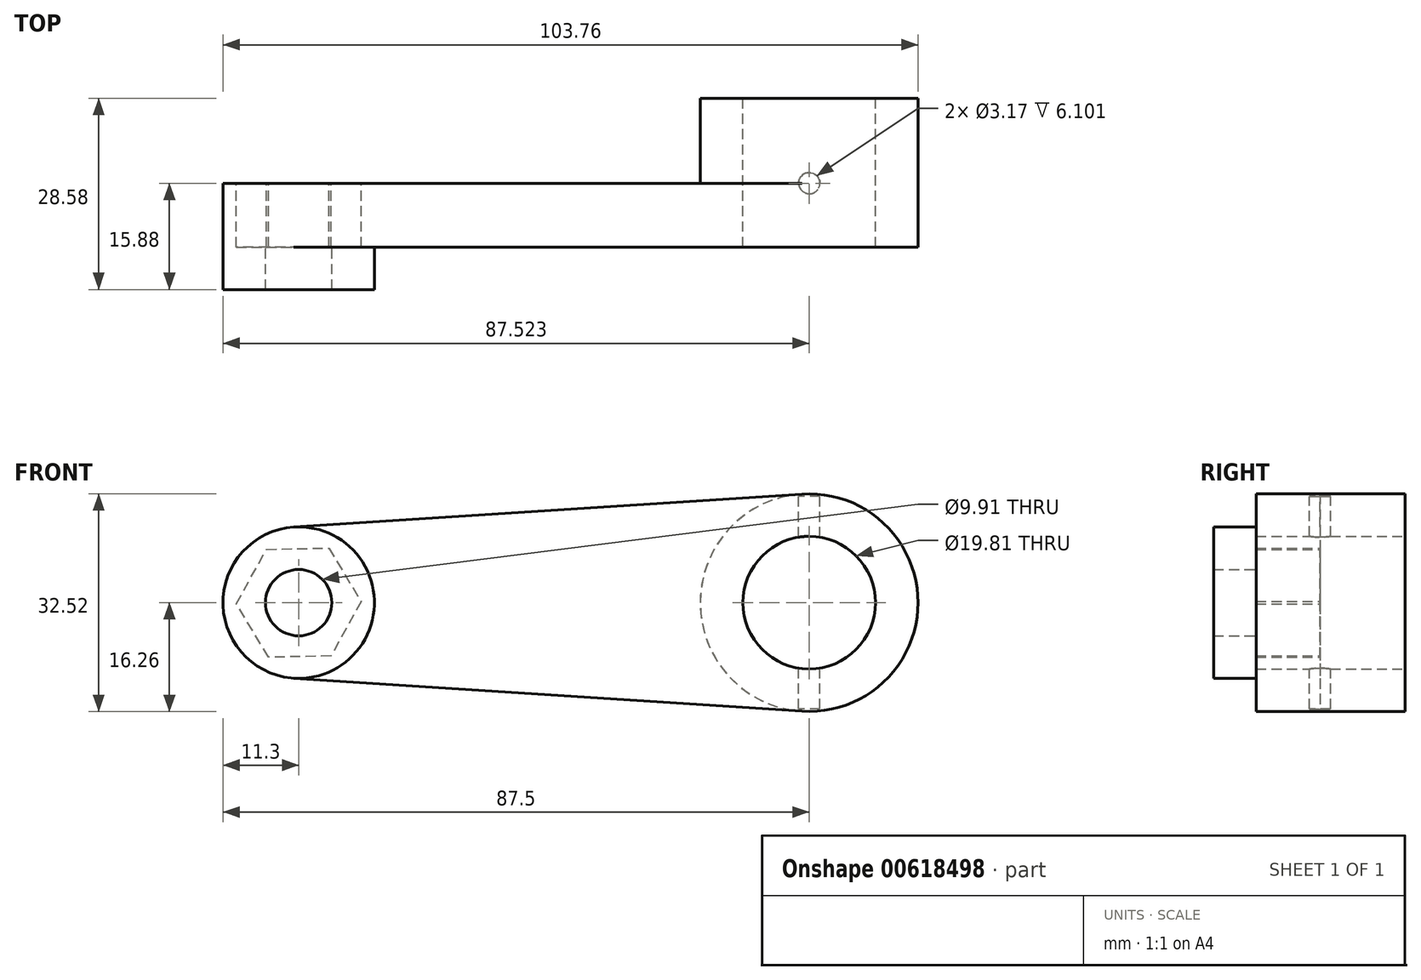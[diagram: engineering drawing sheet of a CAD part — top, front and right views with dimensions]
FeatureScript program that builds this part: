
annotation { "Feature Type Name" : "Feature", "Feature Type Description" : "" }
export const myFeature = defineFeature(function(context is Context, id is Id, definition is map)
    precondition{}
    {
        {
            var Q0;
            Q0=qCreatedBy(makeId("Front.planeOp"),FACE);
            var sketch = newSketch(context, id + "F0", { "sketchPlane" : qUnion([Q0])});
            skCircle(sketch, "E0", {"center": v(0, 0) * mm, "radius": 4.95 * mm});
            skCircle(sketch, "E1", {"center": v(76.2, 0) * mm, "radius": 9.9 * mm});
            skCircle(sketch, "E2.0", {"center": v(0, 0) * mm, "radius": 11.3 * mm});
            skCircle(sketch, "E3.0", {"center": v(76.2, 0) * mm, "radius": 16.26 * mm});
            skLineSegment(sketch, "E4", {"start": v(-0.73, 11.28) * mm, "end": v(75.14, 16.22) * mm});
            skLineSegment(sketch, "E5.MirrorCS", {"start": v(-0.73, -11.28) * mm, "end": v(75.14, -16.22) * mm});
            skSolve(sketch);
        }
        {
            var Q0;
            Q0=makeQuery(id+"F0.imprint","IMPRINT",FACE,{"disambiguationData":[TD([[makeQuery(id+"F0.imprint","IMPRINT",EDGE,{"derivedFrom":sQuery(id+"F0.wireOp",EDGE,"E0")}),-1.0]])]});
            extrude(context, id + "F1", {"entities" : qUnion([Q0]), "depth" : 15.88 * mm, "offsetDistance" : 25.4 * mm});
        }
        {
            var Q0;
            Q0 = qSketchRegion(id + "F0", true);
            extrude(context, id + "F2", {"entities" : qUnion([Q0]), "operationType" : NewBodyOperationType.ADD, "depth" : 9.52 * mm, "offsetDistance" : 25.4 * mm});
        }
        {
            var Q0;
            Q0=makeQuery(id+"F0.imprint","IMPRINT",FACE,{"disambiguationData":[TD([[makeQuery(id+"F0.imprint","IMPRINT",EDGE,{"derivedFrom":sQuery(id+"F0.wireOp",EDGE,"E1")}),-1.0]])]});
            extrude(context, id + "F3", {"entities" : qUnion([Q0]), "operationType" : NewBodyOperationType.ADD, "oppositeDirection" : true, "depth" : 12.7 * mm, "offsetDistance" : 25.4 * mm});
        }
        {
            var Q0;
            Q0=qCreatedBy(makeId("Front.planeOp"),FACE);
            var sketch = newSketch(context, id + "F4", { "sketchPlane" : qUnion([Q0])});
            skCircle(sketch, "E6.cCircle", {"center": v(0, 0) * mm, "radius": 8.06 * mm, "construction": true});
            skLineSegment(sketch, "E6.0", {"start": v(-9.31, -0.2) * mm, "end": v(-4.82, 7.97) * mm});
            skLineSegment(sketch, "E6.1", {"start": v(-4.82, 7.97) * mm, "end": v(4.5, 8.16) * mm});
            skLineSegment(sketch, "E6.2", {"start": v(4.5, 8.16) * mm, "end": v(9.31, 0.2) * mm});
            skLineSegment(sketch, "E6.3", {"start": v(9.31, 0.2) * mm, "end": v(4.82, -7.97) * mm});
            skLineSegment(sketch, "E6.4", {"start": v(4.82, -7.97) * mm, "end": v(-4.5, -8.16) * mm});
            skLineSegment(sketch, "E6.5", {"start": v(-4.5, -8.16) * mm, "end": v(-9.31, -0.2) * mm});
            skPoint(sketch, "E6.0.midPoint", {"position": v(-7.06, 3.89) * mm});
            skSolve(sketch);
        }
        {
            var Q0;
            Q0 = qSketchRegion(id + "F4", true);
            extrude(context, id + "F5", {"entities" : qUnion([Q0]), "operationType" : NewBodyOperationType.REMOVE, "depth" : 9.52 * mm, "offsetDistance" : 25.4 * mm});
        }
        {
            var Q0;
            Q0=qCreatedBy(makeId("Top.planeOp"),FACE);
            var sketch = newSketch(context, id + "F6", { "sketchPlane" : qUnion([Q0])});
            skCircle(sketch, "E7", {"center": v(76.22, 0) * mm, "radius": 1.59 * mm});
            skSolve(sketch);
        }
        {
            var Q0;
            Q0 = qSketchRegion(id + "F6", true);
            extrude(context, id + "F7", {"entities" : qUnion([Q0]), "operationType" : NewBodyOperationType.REMOVE, "endBound" : BoundingType.SYMMETRIC, "oppositeDirection" : true, "depth" : 31.75 * mm, "offsetDistance" : 25.4 * mm});
        }
    });
